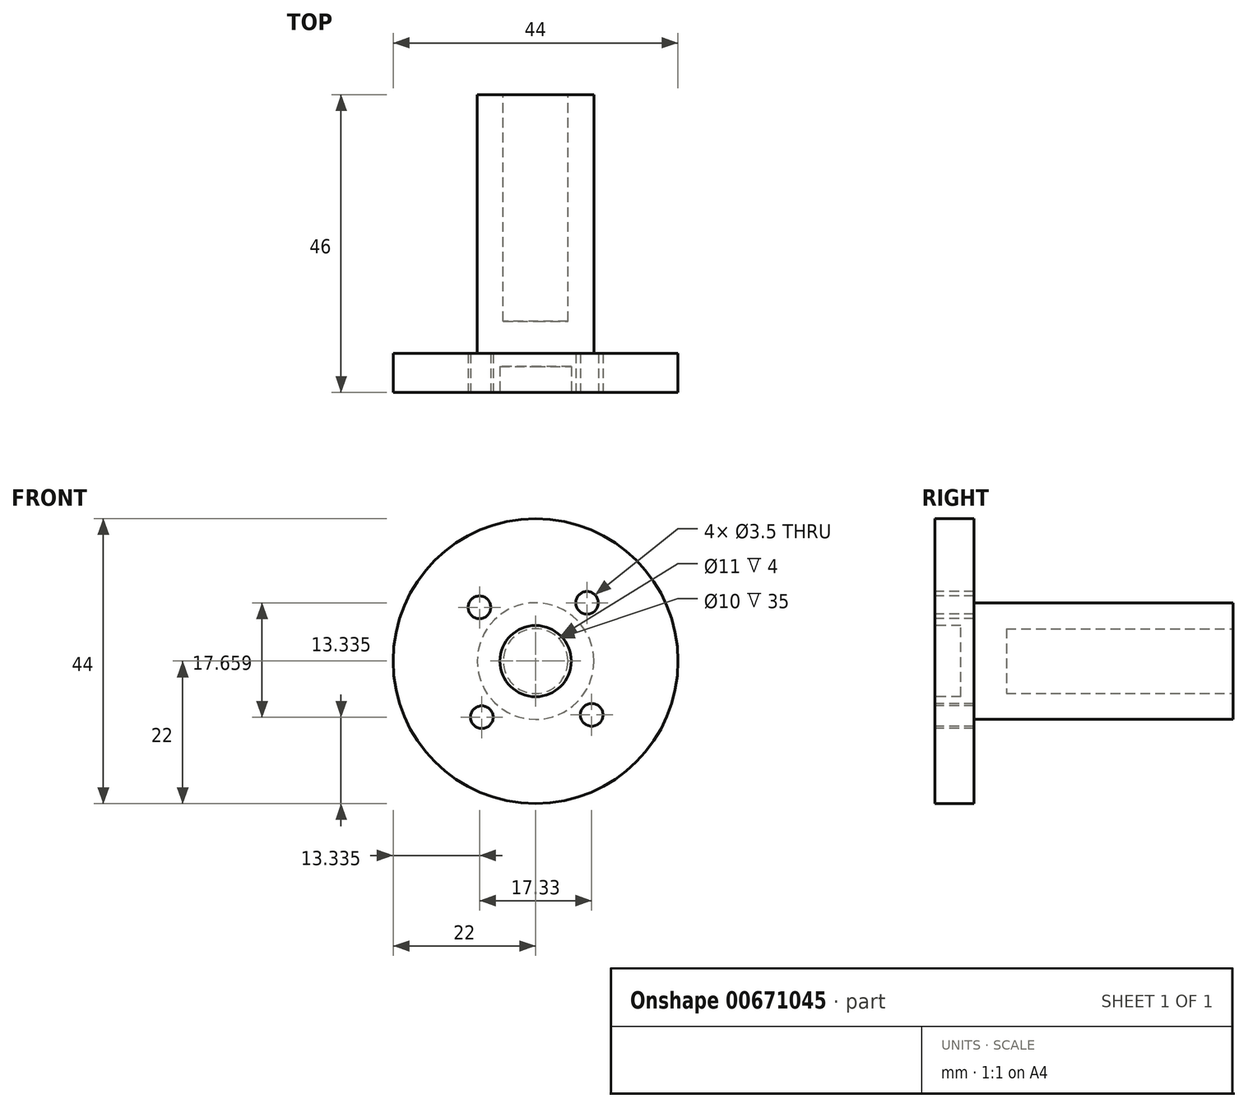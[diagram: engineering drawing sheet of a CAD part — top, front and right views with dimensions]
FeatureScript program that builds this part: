
annotation { "Feature Type Name" : "Feature", "Feature Type Description" : "" }
export const myFeature = defineFeature(function(context is Context, id is Id, definition is map)
    precondition{}
    {
        {
            var Q0;
            Q0=qCreatedBy(makeId("Front.planeOp"),FACE);
            var sketch = newSketch(context, id + "F0", { "sketchPlane" : qUnion([Q0])});
            skCircle(sketch, "E0", {"center": v(0, 0) * mm, "radius": 22 * mm});
            skSolve(sketch);
        }
        {
            var Q0;
            Q0=makeQuery(id+"F0.imprint","IMPRINT",FACE,{"disambiguationData":[TD([[makeQuery(id+"F0.imprint","IMPRINT",EDGE,{"derivedFrom":sQuery(id+"F0.wireOp",EDGE,"E0")}),1.0]])]});
            extrude(context, id + "F1", {"entities" : qUnion([Q0]), "depth" : 6 * mm, "offsetDistance" : 25 * mm});
        }
        {
            var Q0;
            Q0=makeQuery(id+"F1.opExtrude","CAP_FACE",FACE,{"disambiguationData":[OSD([sQuery(id+"F0.wireOp",EDGE,"E0")])],"isStart":false});
            var sketch = newSketch(context, id + "F2", { "sketchPlane" : qUnion([Q0])});
            skCircle(sketch, "E1", {"center": v(0, 0) * mm, "radius": 5.5 * mm});
            skCircle(sketch, "E2", {"center": v(-8.67, 8.3) * mm, "radius": 1.75 * mm});
            skCircle(sketch, "E3", {"center": v(7.94, 9) * mm, "radius": 1.75 * mm});
            skCircle(sketch, "E4", {"center": v(-8.3, -8.67) * mm, "radius": 1.75 * mm});
            skCircle(sketch, "E5", {"center": v(8.67, -8.3) * mm, "radius": 1.75 * mm});
            skLineSegment(sketch, "E6", {"start": v(-15.89, 15.22) * mm, "end": v(0, 0) * mm, "construction": true});
            skLineSegment(sketch, "E7", {"start": v(0, 0) * mm, "end": v(14.56, 16.49) * mm, "construction": true});
            skLineSegment(sketch, "E8", {"start": v(0, 0) * mm, "end": v(-15.22, -15.89) * mm, "construction": true});
            skLineSegment(sketch, "E9", {"start": v(0, 0) * mm, "end": v(15.89, -15.22) * mm, "construction": true});
            skSolve(sketch);
        }
        {
            var Q0;
            Q0=makeQuery(id+"F2.imprint","IMPRINT",FACE,{"disambiguationData":[TD([[makeQuery(id+"F2.imprint","IMPRINT",EDGE,{"derivedFrom":sQuery(id+"F2.wireOp",EDGE,"E4")}),1.0]])]});
            var Q1;
            Q1=makeQuery(id+"F2.imprint","IMPRINT",FACE,{"disambiguationData":[TD([[makeQuery(id+"F2.imprint","IMPRINT",EDGE,{"derivedFrom":sQuery(id+"F2.wireOp",EDGE,"E5")}),1.0]])]});
            var Q2;
            Q2=makeQuery(id+"F2.imprint","IMPRINT",FACE,{"disambiguationData":[TD([[makeQuery(id+"F2.imprint","IMPRINT",EDGE,{"derivedFrom":sQuery(id+"F2.wireOp",EDGE,"E2")}),1.0]])]});
            var Q3;
            Q3=makeQuery(id+"F2.imprint","IMPRINT",FACE,{"disambiguationData":[TD([[makeQuery(id+"F2.imprint","IMPRINT",EDGE,{"derivedFrom":sQuery(id+"F2.wireOp",EDGE,"E3")}),1.0]])]});
            extrude(context, id + "F3", {"entities" : qUnion([Q0, Q1, Q2, Q3]), "operationType" : NewBodyOperationType.REMOVE, "endBound" : BoundingType.THROUGH_ALL, "oppositeDirection" : true, "depth" : 25 * mm, "offsetDistance" : 25 * mm});
        }
        {
            var Q0;
            Q0=makeQuery(id+"F1.opExtrude","CAP_FACE",FACE,{"disambiguationData":[OSD([sQuery(id+"F0.wireOp",EDGE,"E0")])],"isStart":false});
            var sketch = newSketch(context, id + "F4", { "sketchPlane" : qUnion([Q0])});
            skCircle(sketch, "E10", {"center": v(0, 0) * mm, "radius": 5.5 * mm});
            skSolve(sketch);
        }
        {
            var Q0;
            Q0=makeQuery(id+"F4.imprint","IMPRINT",FACE,{"disambiguationData":[TD([[makeQuery(id+"F4.imprint","IMPRINT",EDGE,{"derivedFrom":sQuery(id+"F4.wireOp",EDGE,"E10")}),1.0]])]});
            extrude(context, id + "F5", {"entities" : qUnion([Q0]), "operationType" : NewBodyOperationType.REMOVE, "oppositeDirection" : true, "depth" : 4 * mm, "offsetDistance" : 25 * mm});
        }
        {
            var Q0;
            Q0=makeQuery(id+"F1.opExtrude","CAP_FACE",FACE,{"disambiguationData":[OSD([sQuery(id+"F0.wireOp",EDGE,"E0")])],"isStart":true});
            var sketch = newSketch(context, id + "F6", { "sketchPlane" : qUnion([Q0])});
            skCircle(sketch, "E11", {"center": v(0, 0) * mm, "radius": 9 * mm});
            skSolve(sketch);
        }
        {
            var Q0;
            Q0=makeQuery(id+"F6.imprint","IMPRINT",FACE,{"disambiguationData":[TD([[makeQuery(id+"F6.imprint","IMPRINT",EDGE,{"derivedFrom":sQuery(id+"F6.wireOp",EDGE,"E11")}),1.0]])]});
            extrude(context, id + "F7", {"entities" : qUnion([Q0]), "operationType" : NewBodyOperationType.ADD, "depth" : 40 * mm, "offsetDistance" : 25 * mm});
        }
        {
            var Q0;
            Q0=makeQuery(id+"F7.opExtrude","CAP_FACE",FACE,{"disambiguationData":[OSD([sQuery(id+"F6.wireOp",EDGE,"E11")])],"isStart":false});
            var sketch = newSketch(context, id + "F8", { "sketchPlane" : qUnion([Q0])});
            skCircle(sketch, "E12", {"center": v(0, 0) * mm, "radius": 5 * mm});
            skSolve(sketch);
        }
        {
            var Q0;
            Q0=makeQuery(id+"F8.imprint","IMPRINT",FACE,{"disambiguationData":[TD([[makeQuery(id+"F8.imprint","IMPRINT",EDGE,{"derivedFrom":sQuery(id+"F8.wireOp",EDGE,"E12")}),1.0]])]});
            extrude(context, id + "F9", {"entities" : qUnion([Q0]), "operationType" : NewBodyOperationType.REMOVE, "oppositeDirection" : true, "depth" : 35 * mm, "offsetDistance" : 25 * mm});
        }
    });
